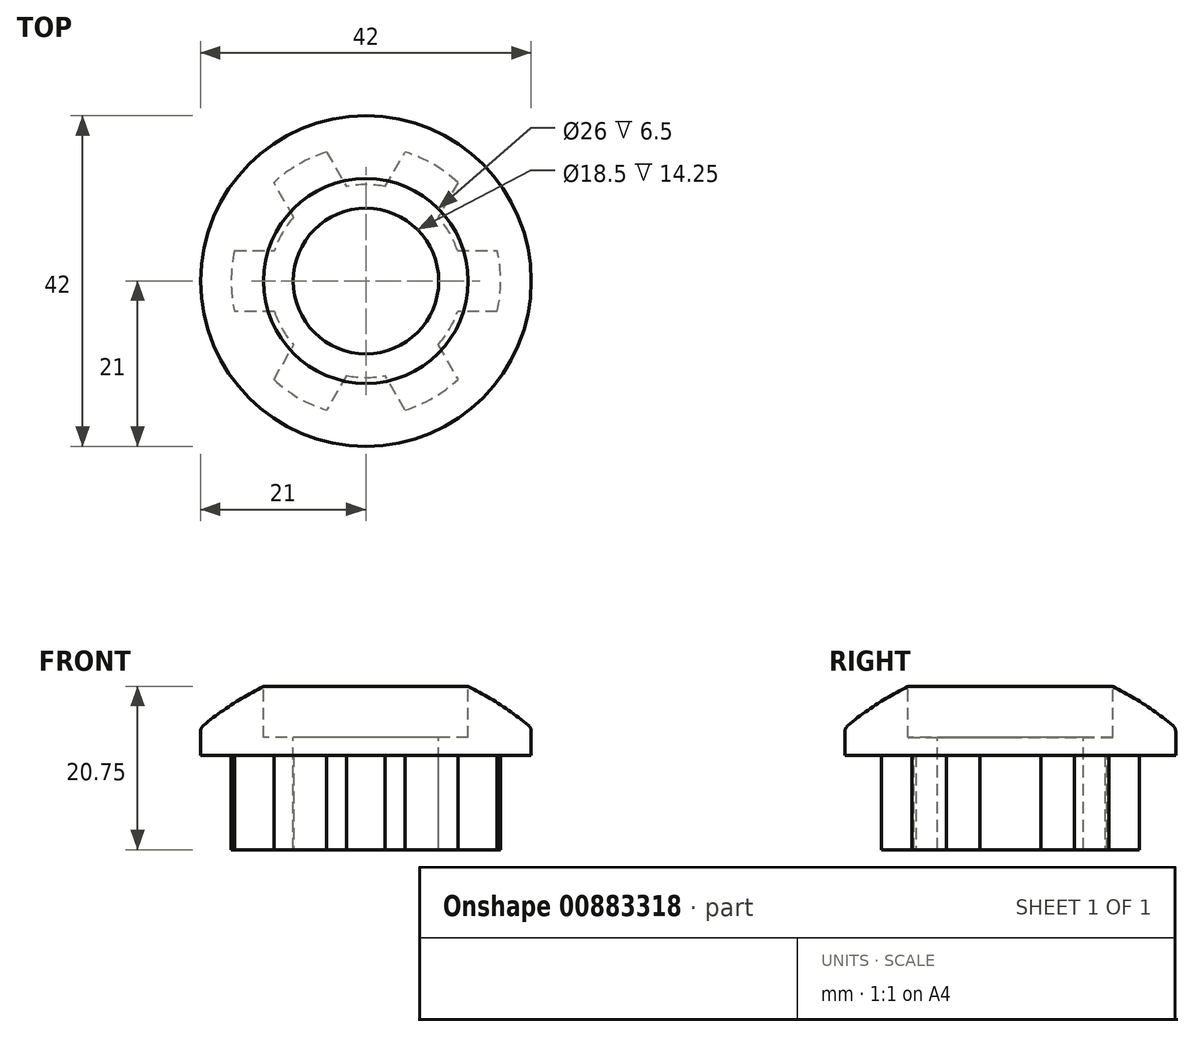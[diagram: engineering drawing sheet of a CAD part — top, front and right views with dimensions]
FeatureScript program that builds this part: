
annotation { "Feature Type Name" : "Feature", "Feature Type Description" : "" }
export const myFeature = defineFeature(function(context is Context, id is Id, definition is map)
    precondition{}
    {
        {
            var Q0;
            Q0=qCreatedBy(makeId("Front.planeOp"),FACE);
            var sketch = newSketch(context, id + "F0", { "sketchPlane" : qUnion([Q0])});
            skLineSegment(sketch, "E0", {"start": v(12.25, 0) * mm, "end": v(12.25, 12) * mm});
            skLineSegment(sketch, "E1", {"start": v(12.25, 12) * mm, "end": v(21, 12) * mm});
            skLineSegment(sketch, "E2", {"start": v(21, 12) * mm, "end": v(21, 15.03) * mm});
            skArc(sketch, "E3", {"start": v(13, 20.75) * mm, "mid": v(16.96, 18.5) * mm, "end": v(20.64, 15.8) * mm});
            skLineSegment(sketch, "E4", {"start": v(0, 0) * mm, "end": v(0, 21.5) * mm});
            skLineSegment(sketch, "E5", {"start": v(0, 37.13) * mm, "end": v(0, 0) * mm, "construction": true});
            skLineSegment(sketch, "E6", {"start": v(12.25, 6.9) * mm, "end": v(12.25, 12) * mm, "construction": true});
            skLineSegment(sketch, "E7", {"start": v(13, 24.44) * mm, "end": v(13, 20.75) * mm, "construction": true});
            skLineSegment(sketch, "E8", {"start": v(13, 20.75) * mm, "end": v(13, 14.25) * mm});
            skLineSegment(sketch, "E9", {"start": v(13, 14.25) * mm, "end": v(9.25, 14.25) * mm});
            skLineSegment(sketch, "E10", {"start": v(12.25, 0) * mm, "end": v(9.25, 0) * mm});
            skLineSegment(sketch, "E11", {"start": v(9.25, 14.25) * mm, "end": v(9.25, 0) * mm});
            skPoint(sketch, "E12.visualSharp", {"position": v(21, 15.5) * mm});
            skArc(sketch, "E12.filletArc", {"start": v(21, 15.03) * mm, "mid": v(20.9, 15.46) * mm, "end": v(20.64, 15.8) * mm});
            skSolve(sketch);
        }
        {
            var Q0;
            Q0 = qSketchRegion(id + "F0", true);
            var Q1;
            Q1=sQuery(id+"F0.wireOp",EDGE,"E5");
            revolve(context, id + "F1", {"surfaceOperationType" : NewSurfaceOperationType.NEW, "entities" : qUnion([Q0]), "axis" : qUnion([Q1]), "revolveType" : RevolveType.FULL});
        }
        {
            var Q0;
            Q0=makeQuery(id+"F1.opRevolve","SWEPT_FACE",FACE,{"disambiguationData":[OSD([sQuery(id+"F0.wireOp",EDGE,"E10")])]});
            var sketch = newSketch(context, id + "F2", { "sketchPlane" : qUnion([Q0])});
            skLineSegment(sketch, "E13", {"start": v(-11.62, 3.87) * mm, "end": v(-17.12, 3.87) * mm});
            skLineSegment(sketch, "E14", {"start": v(-17.12, 3.87) * mm, "end": v(-17.12, -3.87) * mm});
            skLineSegment(sketch, "E15", {"start": v(-17.12, -3.87) * mm, "end": v(-11.62, -3.87) * mm});
            skLineSegment(sketch, "E16.1.0", {"start": v(-9.17, -8.13) * mm, "end": v(-11.92, -12.89) * mm});
            skLineSegment(sketch, "E16.1.1", {"start": v(-11.92, -12.89) * mm, "end": v(-5.2, -16.76) * mm});
            skLineSegment(sketch, "E16.1.2", {"start": v(-5.2, -16.76) * mm, "end": v(-2.45, -12) * mm});
            skLineSegment(sketch, "E16.2.0", {"start": v(2.45, -12) * mm, "end": v(5.2, -16.76) * mm});
            skLineSegment(sketch, "E16.2.1", {"start": v(5.2, -16.76) * mm, "end": v(11.92, -12.89) * mm});
            skLineSegment(sketch, "E16.2.2", {"start": v(11.92, -12.89) * mm, "end": v(9.17, -8.13) * mm});
            skLineSegment(sketch, "E16.3.0", {"start": v(11.62, -3.88) * mm, "end": v(17.12, -3.88) * mm});
            skLineSegment(sketch, "E16.3.1", {"start": v(17.12, -3.88) * mm, "end": v(17.12, 3.87) * mm});
            skLineSegment(sketch, "E16.3.2", {"start": v(17.12, 3.87) * mm, "end": v(11.62, 3.87) * mm});
            skLineSegment(sketch, "E16.4.0", {"start": v(9.17, 8.13) * mm, "end": v(11.92, 12.89) * mm});
            skLineSegment(sketch, "E16.4.1", {"start": v(11.92, 12.89) * mm, "end": v(5.2, 16.76) * mm});
            skLineSegment(sketch, "E16.4.2", {"start": v(5.2, 16.76) * mm, "end": v(2.45, 12) * mm});
            skLineSegment(sketch, "E16.5.0", {"start": v(-2.45, 12) * mm, "end": v(-5.2, 16.76) * mm});
            skLineSegment(sketch, "E16.5.1", {"start": v(-5.2, 16.76) * mm, "end": v(-11.92, 12.89) * mm});
            skLineSegment(sketch, "E16.5.2", {"start": v(-11.92, 12.89) * mm, "end": v(-9.17, 8.13) * mm});
            skPoint(sketch, "E16.center", {"position": v(0, 0) * mm});
            skCircle(sketch, "E17", {"center": v(0, 0) * mm, "radius": 17.12 * mm});
            skSolve(sketch);
        }
        {
            var Q0;
            {var subQ0=sQuery(id+"F2.wireOp",EDGE,"E17");var subQ1=sQuery(id+"F2.wireOp",EDGE,"E13");var subQ2=makeQuery(id+"F2.imprint","INTERSECT",VERTEX,{"derivedFrom":[subQ1,subQ0]});Q0=makeQuery(id+"F2.imprint","IMPRINT",FACE,{"disambiguationData":[TD([[makeQuery(id+"F2.imprint","IMPRINT",EDGE,{"disambiguationData":[TD([[subQ2,-1.0]])],"derivedFrom":subQ0}),1.0]])]});}
            var Q1;
            {var subQ0=sQuery(id+"F2.wireOp",EDGE,"E17");var subQ4=sQuery(id+"F2.wireOp",EDGE,"E16.1.0");var subQ5=makeQuery(id+"F2.imprint","INTERSECT",VERTEX,{"derivedFrom":[subQ4,subQ0]});Q1=makeQuery(id+"F2.imprint","IMPRINT",FACE,{"disambiguationData":[TD([[makeQuery(id+"F2.imprint","IMPRINT",EDGE,{"disambiguationData":[TD([[subQ5,-1.0]])],"derivedFrom":subQ0}),1.0]])]});}
            var Q2;
            {var subQ0=sQuery(id+"F2.wireOp",EDGE,"E17");var subQ4=sQuery(id+"F2.wireOp",EDGE,"E16.2.0");var subQ5=makeQuery(id+"F2.imprint","INTERSECT",VERTEX,{"derivedFrom":[subQ4,subQ0]});Q2=makeQuery(id+"F2.imprint","IMPRINT",FACE,{"disambiguationData":[TD([[makeQuery(id+"F2.imprint","IMPRINT",EDGE,{"disambiguationData":[TD([[subQ5,-1.0]])],"derivedFrom":subQ0}),1.0]])]});}
            var Q3;
            {var subQ0=sQuery(id+"F2.wireOp",EDGE,"E17");var subQ1=makeQuery(id+"F2.imprint","INTERSECT",VERTEX,{"derivedFrom":[sQuery(id+"F2.wireOp",EDGE,"E16.3.1"),subQ0]});Q3=makeQuery(id+"F2.imprint","IMPRINT",FACE,{"disambiguationData":[TD([[makeQuery(id+"F2.imprint","IMPRINT",EDGE,{"disambiguationData":[TD([[subQ1,-1.0]])],"derivedFrom":subQ0}),1.0]])]});}
            var Q4;
            {var subQ0=sQuery(id+"F2.wireOp",EDGE,"E17");var subQ1=sQuery(id+"F2.wireOp",EDGE,"E16.4.0");var subQ2=makeQuery(id+"F2.imprint","INTERSECT",VERTEX,{"derivedFrom":[subQ1,subQ0]});Q4=makeQuery(id+"F2.imprint","IMPRINT",FACE,{"disambiguationData":[TD([[makeQuery(id+"F2.imprint","IMPRINT",EDGE,{"disambiguationData":[TD([[subQ2,-1.0]])],"derivedFrom":subQ0}),1.0]])]});}
            var Q5;
            {var subQ0=sQuery(id+"F2.wireOp",EDGE,"E17");var subQ4=sQuery(id+"F2.wireOp",EDGE,"E16.5.0");var subQ5=makeQuery(id+"F2.imprint","INTERSECT",VERTEX,{"derivedFrom":[subQ4,subQ0]});Q5=makeQuery(id+"F2.imprint","IMPRINT",FACE,{"disambiguationData":[TD([[makeQuery(id+"F2.imprint","IMPRINT",EDGE,{"disambiguationData":[TD([[subQ5,-1.0]])],"derivedFrom":subQ0}),1.0]])]});}
            var Q6;
            Q6=makeQuery(id+"F1.opRevolve","SWEPT_FACE",FACE,{"disambiguationData":[OSD([sQuery(id+"F0.wireOp",EDGE,"E1")])]});
            extrude(context, id + "F3", {"entities" : qUnion([Q0, Q1, Q2, Q3, Q4, Q5]), "operationType" : NewBodyOperationType.ADD, "endBound" : BoundingType.UP_TO_SURFACE, "oppositeDirection" : true, "depth" : 25 * mm, "endBoundEntityFace" : qUnion([Q6]), "offsetDistance" : 25 * mm});
        }
    });
